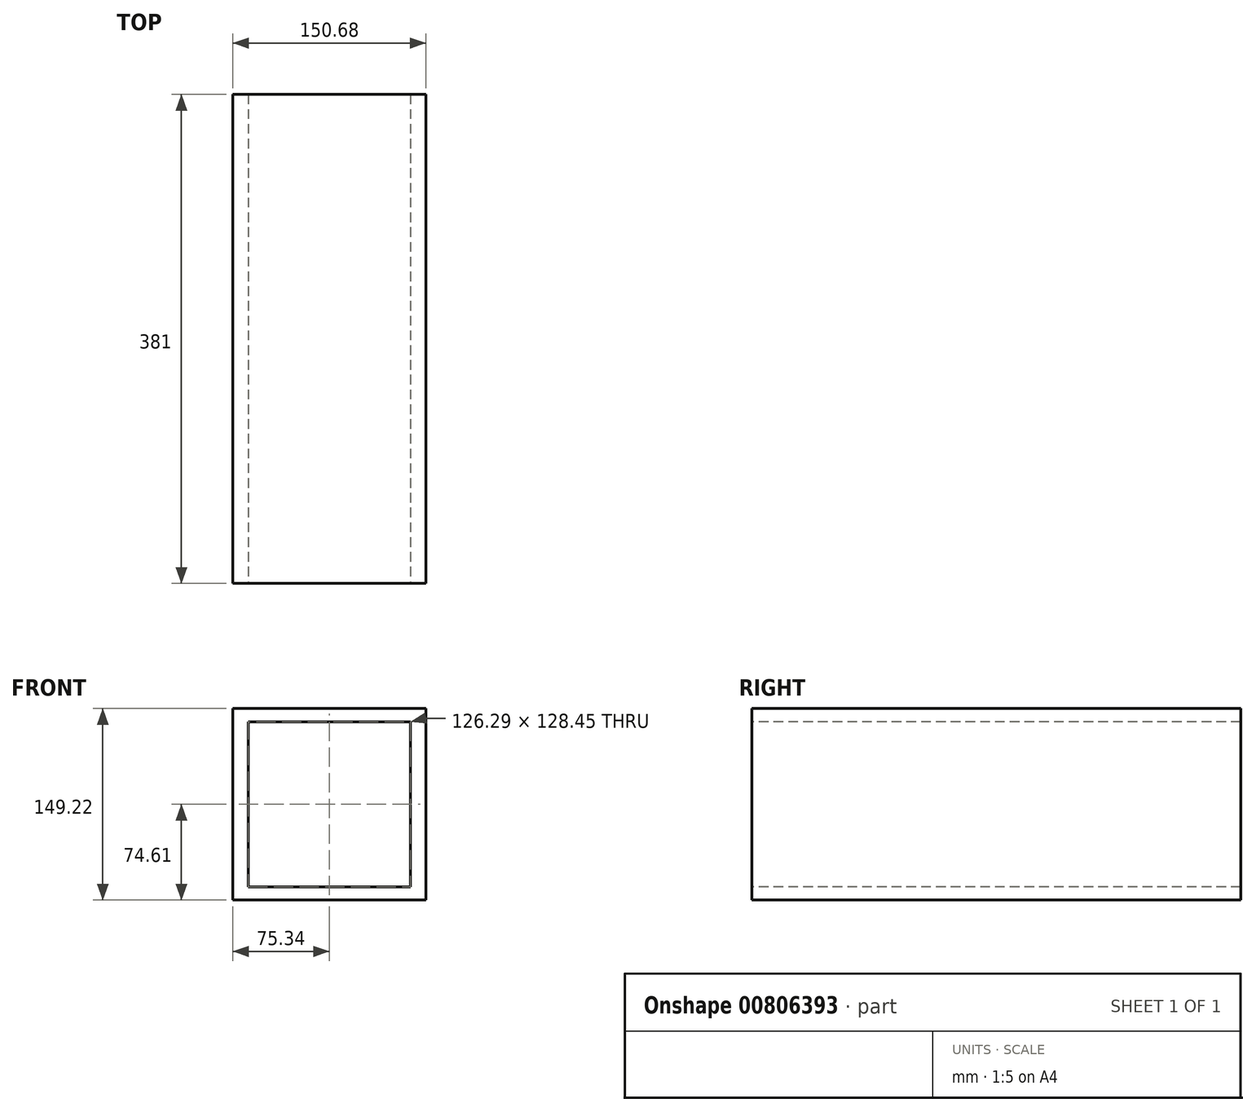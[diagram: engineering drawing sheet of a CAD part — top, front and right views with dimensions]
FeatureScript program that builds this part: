
annotation { "Feature Type Name" : "Feature", "Feature Type Description" : "" }
export const myFeature = defineFeature(function(context is Context, id is Id, definition is map)
    precondition{}
    {
        {
            var Q0;
            Q0=qCreatedBy(makeId("Front.planeOp"),FACE);
            var sketch = newSketch(context, id + "F0", { "sketchPlane" : qUnion([Q0])});
            skLineSegment(sketch, "E0.bottom", {"start": v(0, 0) * mm, "end": v(-76.62, 0) * mm});
            skLineSegment(sketch, "E0.top", {"start": v(0, 73.9) * mm, "end": v(-76.62, 73.9) * mm});
            skLineSegment(sketch, "E0.left", {"start": v(0, 0) * mm, "end": v(0, 73.9) * mm});
            skLineSegment(sketch, "E0.right", {"start": v(-76.62, 0) * mm, "end": v(-76.62, 73.9) * mm});
            skPoint(sketch, "E0.middle", {"position": v(-38.31, 36.95) * mm});
            skLineSegment(sketch, "E1.bottom", {"start": v(75.34, -74.6) * mm, "end": v(-75.34, -74.6) * mm});
            skLineSegment(sketch, "E1.top", {"start": v(75.34, 74.6) * mm, "end": v(-75.34, 74.6) * mm});
            skLineSegment(sketch, "E1.left", {"start": v(75.34, -74.6) * mm, "end": v(75.34, 74.6) * mm});
            skLineSegment(sketch, "E1.right", {"start": v(-75.34, -74.6) * mm, "end": v(-75.34, 74.6) * mm});
            skPoint(sketch, "E1.middle", {"position": v(0, 0) * mm});
            skSolve(sketch);
        }
        {
            var Q0;
            {var subQ1=sQuery(id+"F0.wireOp",EDGE,"E0.left");Q0=makeQuery(id+"F0.imprint","IMPRINT",FACE,{"disambiguationData":[TD([[makeQuery(id+"F0.imprint","IMPRINT",EDGE,{"derivedFrom":subQ1}),-1.0]])]});}
            var Q1;
            {var subQ0=sQuery(id+"F0.wireOp",EDGE,"E0.left");Q1=makeQuery(id+"F0.imprint","IMPRINT",FACE,{"disambiguationData":[TD([[makeQuery(id+"F0.imprint","IMPRINT",EDGE,{"derivedFrom":subQ0}),1.0]])]});}
            extrude(context, id + "F1", {"entities" : qUnion([Q0, Q1]), "endBound" : BoundingType.SYMMETRIC, "depth" : 381 * mm, "offsetDistance" : 25.4 * mm});
        }
        {
            var Q0;
            Q0=makeQuery(id+"F1.opExtrude","CAP_FACE",FACE,{"disambiguationData":[OSD([sQuery(id+"F0.wireOp",EDGE,"E1.bottom"),sQuery(id+"F0.wireOp",EDGE,"E1.top"),sQuery(id+"F0.wireOp",EDGE,"E1.left"),sQuery(id+"F0.wireOp",EDGE,"E1.right")])],"isStart":false});
            var sketch = newSketch(context, id + "F2", { "sketchPlane" : qUnion([Q0])});
            skLineSegment(sketch, "E2.bottom", {"start": v(-63.14, -64.22) * mm, "end": v(63.14, -64.22) * mm});
            skLineSegment(sketch, "E2.top", {"start": v(-63.14, 64.22) * mm, "end": v(63.14, 64.22) * mm});
            skLineSegment(sketch, "E2.left", {"start": v(-63.14, -64.22) * mm, "end": v(-63.14, 64.22) * mm});
            skLineSegment(sketch, "E2.right", {"start": v(63.14, -64.22) * mm, "end": v(63.14, 64.22) * mm});
            skPoint(sketch, "E2.middle", {"position": v(0, 0) * mm});
            skSolve(sketch);
        }
        {
            var Q0;
            Q0=makeQuery(id+"F2.imprint","IMPRINT",FACE,{"disambiguationData":[TD([[makeQuery(id+"F2.imprint","IMPRINT",EDGE,{"derivedFrom":sQuery(id+"F2.wireOp",EDGE,"E2.bottom")}),1.0]])]});
            extrude(context, id + "F3", {"entities" : qUnion([Q0]), "operationType" : NewBodyOperationType.REMOVE, "oppositeDirection" : true, "depth" : 482.6 * mm, "offsetDistance" : 25.4 * mm});
        }
    });
